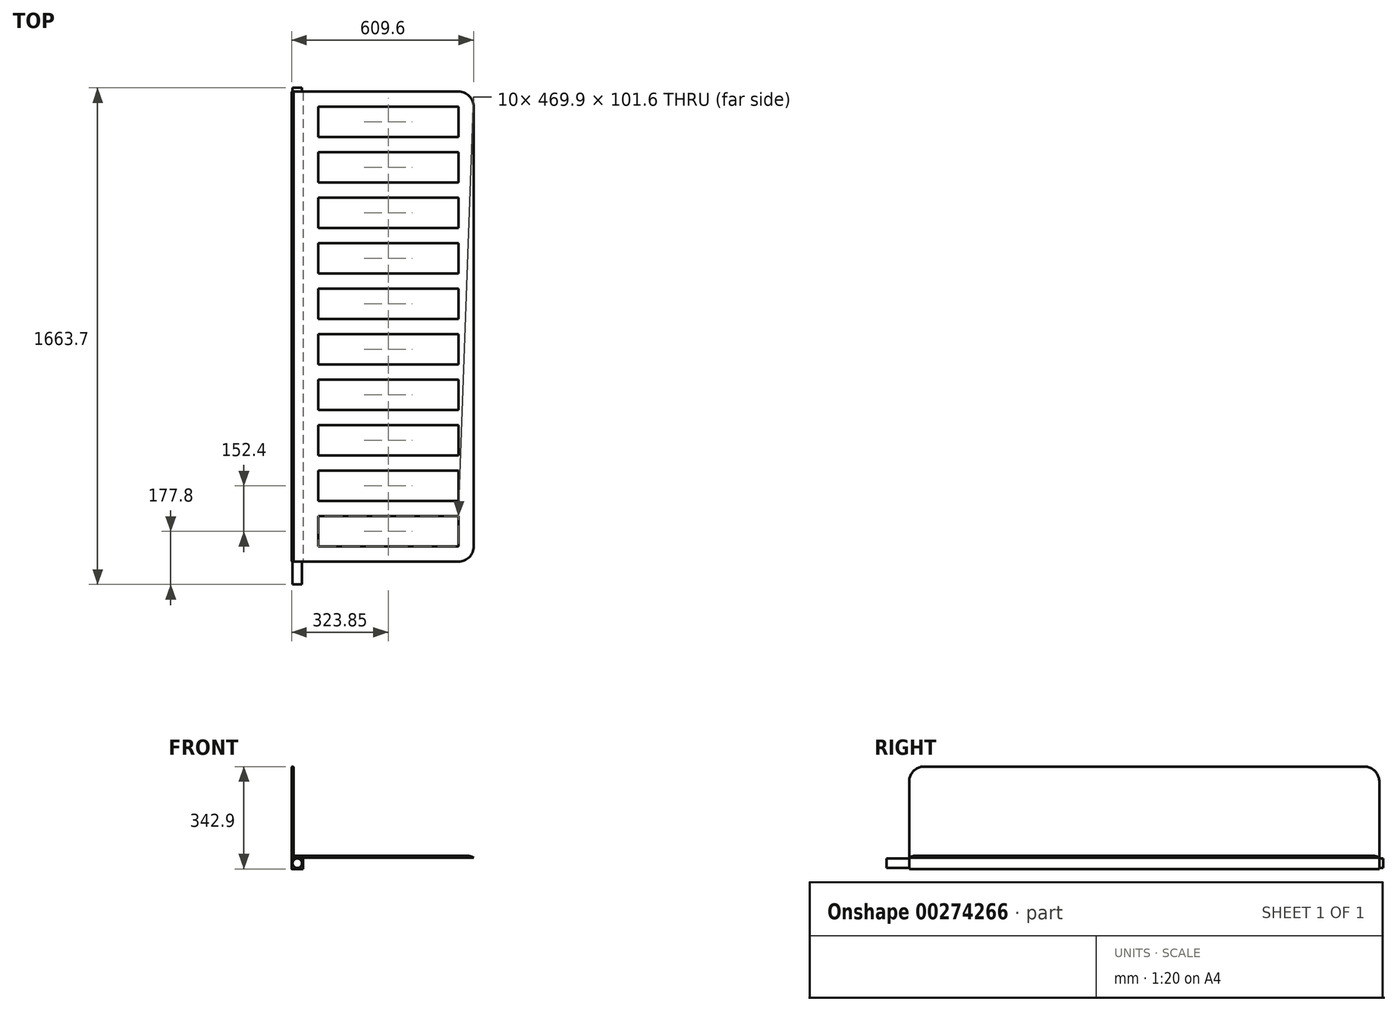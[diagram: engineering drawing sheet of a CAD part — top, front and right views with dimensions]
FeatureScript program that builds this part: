
annotation { "Feature Type Name" : "Feature", "Feature Type Description" : "" }
export const myFeature = defineFeature(function(context is Context, id is Id, definition is map)
    precondition{}
    {
        {
            var Q0;
            Q0=qCreatedBy(makeId("Front.planeOp"),FACE);
            var sketch = newSketch(context, id + "F0", { "sketchPlane" : qUnion([Q0])});
            skLineSegment(sketch, "E0.bottom", {"start": v(0, 0) * mm, "end": v(609.6, 0) * mm});
            skLineSegment(sketch, "E0.top", {"start": v(0, 6.35) * mm, "end": v(609.6, 6.35) * mm});
            skLineSegment(sketch, "E0.left", {"start": v(0, 0) * mm, "end": v(0, 6.35) * mm});
            skLineSegment(sketch, "E0.right", {"start": v(609.6, 0) * mm, "end": v(609.6, 6.35) * mm});
            skLineSegment(sketch, "E1.bottom", {"start": v(0, 0) * mm, "end": v(6.35, 0) * mm});
            skLineSegment(sketch, "E1.top", {"start": v(0, 304.8) * mm, "end": v(6.35, 304.8) * mm});
            skLineSegment(sketch, "E1.left", {"start": v(0, 0) * mm, "end": v(0, 304.8) * mm});
            skLineSegment(sketch, "E1.right", {"start": v(6.35, 0) * mm, "end": v(6.35, 304.8) * mm});
            skSolve(sketch);
        }
        {
            var Q0;
            {var subQ5=sQuery(id+"F0.wireOp",EDGE,"E1.top");Q0=makeQuery(id+"F0.imprint","IMPRINT",FACE,{"disambiguationData":[TD([[makeQuery(id+"F0.imprint","IMPRINT",EDGE,{"derivedFrom":subQ5}),-1.0]])]});}
            var Q1;
            {var subQ0=sQuery(id+"F0.wireOp",EDGE,"E0.bottom");Q1=makeQuery(id+"F0.imprint","IMPRINT",FACE,{"disambiguationData":[TD([[makeQuery(id+"F0.imprint","IMPRINT",EDGE,{"derivedFrom":subQ0}),1.0]])]});}
            var Q2;
            {var subQ5=sQuery(id+"F0.wireOp",EDGE,"E1.bottom");Q2=makeQuery(id+"F0.imprint","IMPRINT",FACE,{"disambiguationData":[TD([[makeQuery(id+"F0.imprint","IMPRINT",EDGE,{"derivedFrom":subQ5}),1.0]])]});}
            extrude(context, id + "F1", {"entities" : qUnion([Q0, Q1, Q2]), "depth" : 1574.8 * mm});
        }
        {
            var Q0;
            Q0=makeQuery(id+"F1.opExtrude","CAP_FACE",FACE,{"disambiguationData":[OSD([sQuery(id+"F0.wireOp",EDGE,"E0.bottom"),sQuery(id+"F0.wireOp",EDGE,"E0.top"),sQuery(id+"F0.wireOp",EDGE,"E0.right"),sQuery(id+"F0.wireOp",EDGE,"E1.bottom"),sQuery(id+"F0.wireOp",EDGE,"E1.top"),sQuery(id+"F0.wireOp",EDGE,"E1.left"),sQuery(id+"F0.wireOp",EDGE,"E1.right")])],"isStart":false});
            var sketch = newSketch(context, id + "F2", { "sketchPlane" : qUnion([Q0])});
            skLineSegment(sketch, "E2.bottom", {"start": v(0, 0) * mm, "end": v(38.1, 0) * mm});
            skLineSegment(sketch, "E2.top", {"start": v(0, -38.1) * mm, "end": v(38.1, -38.1) * mm});
            skLineSegment(sketch, "E2.left", {"start": v(0, 0) * mm, "end": v(0, -38.1) * mm});
            skLineSegment(sketch, "E2.right", {"start": v(38.1, 0) * mm, "end": v(38.1, -38.1) * mm});
            skSolve(sketch);
        }
        {
            var Q0;
            Q0=makeQuery(id+"F2.imprint","IMPRINT",FACE,{"disambiguationData":[TD([[makeQuery(id+"F2.imprint","IMPRINT",EDGE,{"derivedFrom":sQuery(id+"F2.wireOp",EDGE,"E2.bottom")}),-1.0]])]});
            extrude(context, id + "F3", {"entities" : qUnion([Q0]), "operationType" : NewBodyOperationType.ADD, "oppositeDirection" : true, "depth" : 1574.8 * mm});
        }
        {
            var Q0;
            Q0=makeQuery(id+"F3.boolean.opBoolean","MERGE",FACE,{"derivedFrom":[makeQuery(id+"F1.opExtrude","CAP_FACE",FACE,{"disambiguationData":[OSD([sQuery(id+"F0.wireOp",EDGE,"E0.bottom"),sQuery(id+"F0.wireOp",EDGE,"E0.top"),sQuery(id+"F0.wireOp",EDGE,"E0.right"),sQuery(id+"F0.wireOp",EDGE,"E1.bottom"),sQuery(id+"F0.wireOp",EDGE,"E1.top"),sQuery(id+"F0.wireOp",EDGE,"E1.left"),sQuery(id+"F0.wireOp",EDGE,"E1.right")])],"isStart":false}),makeQuery(id+"F3.opExtrude","CAP_FACE",FACE,{"disambiguationData":[OSD([sQuery(id+"F2.wireOp",EDGE,"TUILDfYx-NHmr-r6Di-cHKC-nHDSRs35YgXG.bottom"),sQuery(id+"F2.wireOp",EDGE,"TUILDfYx-NHmr-r6Di-cHKC-nHDSRs35YgXG.top"),sQuery(id+"F2.wireOp",EDGE,"TUILDfYx-NHmr-r6Di-cHKC-nHDSRs35YgXG.left"),sQuery(id+"F2.wireOp",EDGE,"TUILDfYx-NHmr-r6Di-cHKC-nHDSRs35YgXG.right")])],"isStart":true})]});
            var sketch = newSketch(context, id + "F4", { "sketchPlane" : qUnion([Q0])});
            skPoint(sketch, "E3", {"position": v(19.05, -19.05) * mm});
            skCircle(sketch, "E4", {"center": v(19.05, -19.05) * mm, "radius": 15.88 * mm});
            skSolve(sketch);
        }
        {
            var Q0;
            Q0=makeQuery(id+"F4.imprint","IMPRINT",FACE,{"disambiguationData":[TD([[makeQuery(id+"F4.imprint","IMPRINT",EDGE,{"derivedFrom":sQuery(id+"F4.wireOp",EDGE,"E4")}),1.0]])]});
            extrude(context, id + "F5", {"entities" : qUnion([Q0]), "operationType" : NewBodyOperationType.ADD, "depth" : 76.2 * mm});
        }
        {
            var Q0;
            Q0=makeQuery(id+"F3.boolean.opBoolean","MERGE",FACE,{"derivedFrom":[makeQuery(id+"F1.opExtrude","CAP_FACE",FACE,{"disambiguationData":[OSD([sQuery(id+"F0.wireOp",EDGE,"E0.bottom"),sQuery(id+"F0.wireOp",EDGE,"E0.top"),sQuery(id+"F0.wireOp",EDGE,"E0.right"),sQuery(id+"F0.wireOp",EDGE,"E1.bottom"),sQuery(id+"F0.wireOp",EDGE,"E1.top"),sQuery(id+"F0.wireOp",EDGE,"E1.left"),sQuery(id+"F0.wireOp",EDGE,"E1.right")])],"isStart":true}),makeQuery(id+"F3.opExtrude","CAP_FACE",FACE,{"disambiguationData":[OSD([sQuery(id+"F2.wireOp",EDGE,"TUILDfYx-NHmr-r6Di-cHKC-nHDSRs35YgXG.bottom"),sQuery(id+"F2.wireOp",EDGE,"TUILDfYx-NHmr-r6Di-cHKC-nHDSRs35YgXG.top"),sQuery(id+"F2.wireOp",EDGE,"TUILDfYx-NHmr-r6Di-cHKC-nHDSRs35YgXG.left"),sQuery(id+"F2.wireOp",EDGE,"TUILDfYx-NHmr-r6Di-cHKC-nHDSRs35YgXG.right")])],"isStart":false})]});
            var sketch = newSketch(context, id + "F6", { "sketchPlane" : qUnion([Q0])});
            skCircle(sketch, "E5", {"center": v(-19.05, -19.05) * mm, "radius": 15.88 * mm});
            skSolve(sketch);
        }
        {
            var Q0;
            Q0=makeQuery(id+"F6.imprint","IMPRINT",FACE,{"disambiguationData":[TD([[makeQuery(id+"F6.imprint","IMPRINT",EDGE,{"derivedFrom":sQuery(id+"F6.wireOp",EDGE,"E5")}),1.0]])]});
            extrude(context, id + "F7", {"entities" : qUnion([Q0]), "operationType" : NewBodyOperationType.ADD, "depth" : 12.7 * mm});
        }
        {
            var Q0;
            Q0=makeQuery(id+"F1.opExtrude","SWEPT_FACE",FACE,{"disambiguationData":[OSD([sQuery(id+"F0.wireOp",EDGE,"E0.bottom"),sQuery(id+"F0.wireOp",EDGE,"E1.bottom")])]});
            var sketch = newSketch(context, id + "F8", { "sketchPlane" : qUnion([Q0])});
            skLineSegment(sketch, "E6.bottom", {"start": v(88.9, 1524) * mm, "end": v(558.8, 1524) * mm});
            skLineSegment(sketch, "E6.top", {"start": v(88.9, 1422.4) * mm, "end": v(558.8, 1422.4) * mm});
            skLineSegment(sketch, "E6.left", {"start": v(88.9, 1524) * mm, "end": v(88.9, 1422.4) * mm});
            skLineSegment(sketch, "E6.right", {"start": v(558.8, 1524) * mm, "end": v(558.8, 1422.4) * mm});
            skLineSegment(sketch, "E7.bottom", {"start": v(88.9, 1371.6) * mm, "end": v(558.8, 1371.6) * mm});
            skLineSegment(sketch, "E7.top", {"start": v(88.9, 1270) * mm, "end": v(558.8, 1270) * mm});
            skLineSegment(sketch, "E7.left", {"start": v(88.9, 1371.6) * mm, "end": v(88.9, 1270) * mm});
            skLineSegment(sketch, "E7.right", {"start": v(558.8, 1371.6) * mm, "end": v(558.8, 1270) * mm});
            skLineSegment(sketch, "E8.bottom", {"start": v(88.9, 1219.2) * mm, "end": v(558.8, 1219.2) * mm});
            skLineSegment(sketch, "E8.top", {"start": v(88.9, 1117.6) * mm, "end": v(558.8, 1117.6) * mm});
            skLineSegment(sketch, "E8.left", {"start": v(88.9, 1219.2) * mm, "end": v(88.9, 1117.6) * mm});
            skLineSegment(sketch, "E8.right", {"start": v(558.8, 1219.2) * mm, "end": v(558.8, 1117.6) * mm});
            skLineSegment(sketch, "E9.bottom", {"start": v(558.8, 1066.8) * mm, "end": v(88.9, 1066.8) * mm});
            skLineSegment(sketch, "E9.top", {"start": v(558.8, 965.2) * mm, "end": v(88.9, 965.2) * mm});
            skLineSegment(sketch, "E9.left", {"start": v(558.8, 1066.8) * mm, "end": v(558.8, 965.2) * mm});
            skLineSegment(sketch, "E9.right", {"start": v(88.9, 1066.8) * mm, "end": v(88.9, 965.2) * mm});
            skLineSegment(sketch, "E10.bottom", {"start": v(558.8, 914.4) * mm, "end": v(88.9, 914.4) * mm});
            skLineSegment(sketch, "E10.top", {"start": v(558.8, 812.8) * mm, "end": v(88.9, 812.8) * mm});
            skLineSegment(sketch, "E10.left", {"start": v(558.8, 914.4) * mm, "end": v(558.8, 812.8) * mm});
            skLineSegment(sketch, "E10.right", {"start": v(88.9, 914.4) * mm, "end": v(88.9, 812.8) * mm});
            skLineSegment(sketch, "E11.bottom", {"start": v(558.8, 152.4) * mm, "end": v(88.9, 152.4) * mm});
            skLineSegment(sketch, "E11.top", {"start": v(558.8, 50.8) * mm, "end": v(88.9, 50.8) * mm});
            skLineSegment(sketch, "E11.left", {"start": v(558.8, 152.4) * mm, "end": v(558.8, 50.8) * mm});
            skLineSegment(sketch, "E11.right", {"start": v(88.9, 152.4) * mm, "end": v(88.9, 50.8) * mm});
            skLineSegment(sketch, "E12.bottom", {"start": v(88.9, 203.2) * mm, "end": v(558.8, 203.2) * mm});
            skLineSegment(sketch, "E12.top", {"start": v(88.9, 304.8) * mm, "end": v(558.8, 304.8) * mm});
            skLineSegment(sketch, "E12.left", {"start": v(88.9, 203.2) * mm, "end": v(88.9, 304.8) * mm});
            skLineSegment(sketch, "E12.right", {"start": v(558.8, 203.2) * mm, "end": v(558.8, 304.8) * mm});
            skLineSegment(sketch, "E13.bottom", {"start": v(558.8, 355.6) * mm, "end": v(88.9, 355.6) * mm});
            skLineSegment(sketch, "E13.top", {"start": v(558.8, 457.2) * mm, "end": v(88.9, 457.2) * mm});
            skLineSegment(sketch, "E13.left", {"start": v(558.8, 355.6) * mm, "end": v(558.8, 457.2) * mm});
            skLineSegment(sketch, "E13.right", {"start": v(88.9, 355.6) * mm, "end": v(88.9, 457.2) * mm});
            skLineSegment(sketch, "E14.bottom", {"start": v(558.8, 508) * mm, "end": v(88.9, 508) * mm});
            skLineSegment(sketch, "E14.top", {"start": v(558.8, 609.6) * mm, "end": v(88.9, 609.6) * mm});
            skLineSegment(sketch, "E14.left", {"start": v(558.8, 508) * mm, "end": v(558.8, 609.6) * mm});
            skLineSegment(sketch, "E14.right", {"start": v(88.9, 508) * mm, "end": v(88.9, 609.6) * mm});
            skLineSegment(sketch, "E15.bottom", {"start": v(558.8, 660.4) * mm, "end": v(88.9, 660.4) * mm});
            skLineSegment(sketch, "E15.top", {"start": v(558.8, 762) * mm, "end": v(88.9, 762) * mm});
            skLineSegment(sketch, "E15.left", {"start": v(558.8, 660.4) * mm, "end": v(558.8, 762) * mm});
            skLineSegment(sketch, "E15.right", {"start": v(88.9, 660.4) * mm, "end": v(88.9, 762) * mm});
            skSolve(sketch);
        }
        {
            var Q0;
            Q0=makeQuery(id+"F8.imprint","IMPRINT",FACE,{"disambiguationData":[TD([[makeQuery(id+"F8.imprint","IMPRINT",EDGE,{"derivedFrom":sQuery(id+"F8.wireOp",EDGE,"E6.bottom")}),-1.0]])]});
            var Q1;
            Q1=makeQuery(id+"F8.imprint","IMPRINT",FACE,{"disambiguationData":[TD([[makeQuery(id+"F8.imprint","IMPRINT",EDGE,{"derivedFrom":sQuery(id+"F8.wireOp",EDGE,"E7.bottom")}),-1.0]])]});
            var Q2;
            Q2=makeQuery(id+"F8.imprint","IMPRINT",FACE,{"disambiguationData":[TD([[makeQuery(id+"F8.imprint","IMPRINT",EDGE,{"derivedFrom":sQuery(id+"F8.wireOp",EDGE,"E8.bottom")}),-1.0]])]});
            var Q3;
            Q3=makeQuery(id+"F8.imprint","IMPRINT",FACE,{"disambiguationData":[TD([[makeQuery(id+"F8.imprint","IMPRINT",EDGE,{"derivedFrom":sQuery(id+"F8.wireOp",EDGE,"E9.bottom")}),1.0]])]});
            var Q4;
            Q4=makeQuery(id+"F8.imprint","IMPRINT",FACE,{"disambiguationData":[TD([[makeQuery(id+"F8.imprint","IMPRINT",EDGE,{"derivedFrom":sQuery(id+"F8.wireOp",EDGE,"E10.bottom")}),1.0]])]});
            var Q5;
            Q5=makeQuery(id+"F8.imprint","IMPRINT",FACE,{"disambiguationData":[TD([[makeQuery(id+"F8.imprint","IMPRINT",EDGE,{"derivedFrom":sQuery(id+"F8.wireOp",EDGE,"E15.bottom")}),-1.0]])]});
            var Q6;
            Q6=makeQuery(id+"F8.imprint","IMPRINT",FACE,{"disambiguationData":[TD([[makeQuery(id+"F8.imprint","IMPRINT",EDGE,{"derivedFrom":sQuery(id+"F8.wireOp",EDGE,"E14.bottom")}),-1.0]])]});
            var Q7;
            Q7=makeQuery(id+"F8.imprint","IMPRINT",FACE,{"disambiguationData":[TD([[makeQuery(id+"F8.imprint","IMPRINT",EDGE,{"derivedFrom":sQuery(id+"F8.wireOp",EDGE,"E13.bottom")}),-1.0]])]});
            var Q8;
            Q8=makeQuery(id+"F8.imprint","IMPRINT",FACE,{"disambiguationData":[TD([[makeQuery(id+"F8.imprint","IMPRINT",EDGE,{"derivedFrom":sQuery(id+"F8.wireOp",EDGE,"E12.bottom")}),1.0]])]});
            var Q9;
            Q9=makeQuery(id+"F8.imprint","IMPRINT",FACE,{"disambiguationData":[TD([[makeQuery(id+"F8.imprint","IMPRINT",EDGE,{"derivedFrom":sQuery(id+"F8.wireOp",EDGE,"E11.bottom")}),1.0]])]});
            extrude(context, id + "F9", {"entities" : qUnion([Q0, Q1, Q2, Q3, Q4, Q5, Q6, Q7, Q8, Q9]), "operationType" : NewBodyOperationType.REMOVE, "oppositeDirection" : true, "depth" : 25.4 * mm});
        }
        {
            var Q0;
            Q0=makeQuery(id+"F1.opExtrude","CAP_EDGE",EDGE,{"disambiguationData":[OSD([sQuery(id+"F0.wireOp",EDGE,"E0.right")])],"isStart":true});
            var Q1;
            Q1=makeQuery(id+"F1.opExtrude","CAP_EDGE",EDGE,{"disambiguationData":[OSD([sQuery(id+"F0.wireOp",EDGE,"E0.right")])],"isStart":false});
            var Q2;
            Q2=makeQuery(id+"F1.opExtrude","CAP_EDGE",EDGE,{"disambiguationData":[OSD([sQuery(id+"F0.wireOp",EDGE,"E1.top")])],"isStart":false});
            var Q3;
            Q3=makeQuery(id+"F1.opExtrude","CAP_EDGE",EDGE,{"disambiguationData":[OSD([sQuery(id+"F0.wireOp",EDGE,"E1.top")])],"isStart":true});
            fillet(context, id + "F10", {"entities" : qUnion([Q0, Q1, Q2, Q3]), "radius" : 50.8 * mm, "tangentPropagation" : true, "allowEdgeOverflow" : false});
        }
        {
            var Q0;
            Q0=makeQuery(id+"F1.opExtrude","SWEPT_EDGE",EDGE,{"disambiguationData":[OSD([sQuery(id+"F0.wireOp",EDGE,"E0.top"),sQuery(id+"F0.wireOp",EDGE,"E0.right")])]});
            fillet(context, id + "F11", {"entities" : qUnion([Q0]), "radius" : 50.8 * mm, "tangentPropagation" : true, "allowEdgeOverflow" : false});
        }
        {
            var Q0;
            Q0=makeQuery(id+"F1.opExtrude","SWEPT_EDGE",EDGE,{"disambiguationData":[OSD([sQuery(id+"F0.wireOp",EDGE,"E1.top"),sQuery(id+"F0.wireOp",EDGE,"E1.right")])]});
            var Q1;
            Q1=makeQuery(id+"F1.opExtrude","SWEPT_EDGE",EDGE,{"disambiguationData":[OSD([sQuery(id+"F0.wireOp",EDGE,"E1.top"),sQuery(id+"F0.wireOp",EDGE,"E1.left")])]});
            fillet(context, id + "F12", {"entities" : qUnion([Q0, Q1]), "radius" : 3.17 * mm, "tangentPropagation" : true, "allowEdgeOverflow" : false});
        }
    });
